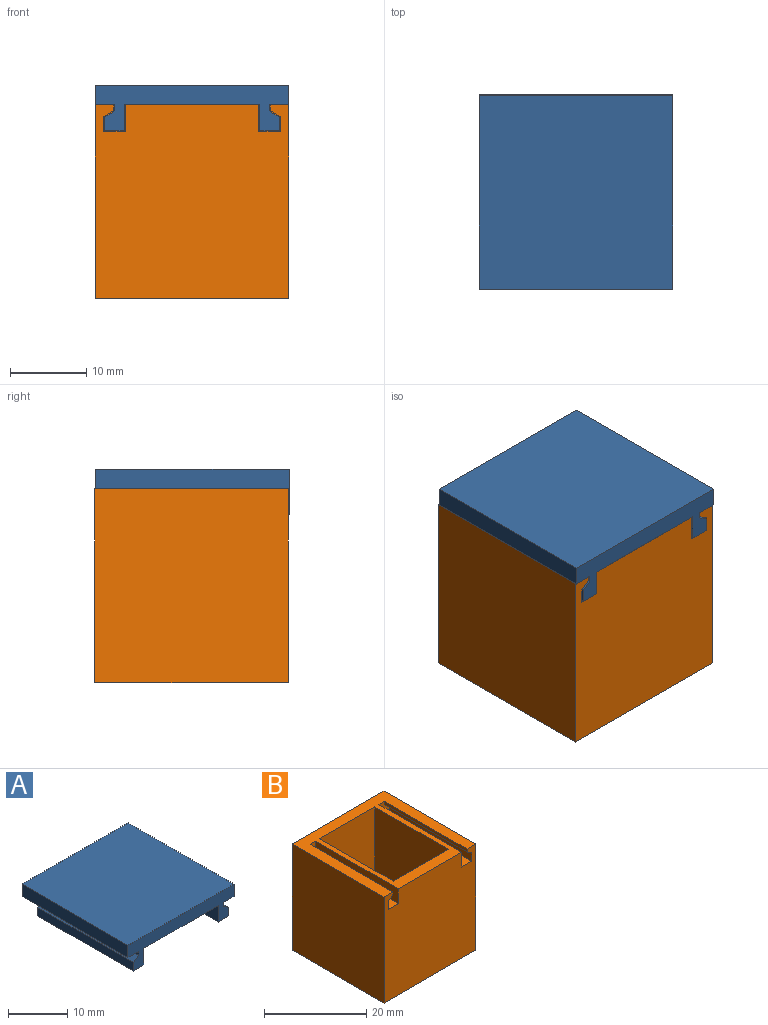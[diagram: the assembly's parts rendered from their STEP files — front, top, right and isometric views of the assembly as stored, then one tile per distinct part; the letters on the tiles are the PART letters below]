
ASSEMBLY  parts=2 mates=1
PART A: 18 faces, bbox 25.4x25.4x6 mm
  f0: plane 25.4x2.54mm, normal (0,1,0), area 64.5mm2, adj f1,f2,f4,f5
  f1: plane 25.4x2.54mm, normal (1,0,0), area 64.5mm2, adj f0,f3,f4,f5
  f2: plane 25.4x2.54mm, normal (-1,0,0), area 64.5mm2, adj f0,f3,f4,f5
  f3: plane 25.4x5.97mm, normal (0,-1,0), area 78.8mm2, adj f1,f2,f4,f5,f6,f7,f8,f9
  f4: plane 25.4x25.4mm, normal (0,0,-1), area 587.1mm2, adj f0,f1,f2,f3,f8,f9,f14,f15
  f5: plane 25.4x25.4mm, normal (0,0,1), area 645.2mm2, adj f0,f1,f2,f3
  f6: plane 22.86x1.78mm, normal (-1,0,0), area 40.6mm2, adj f3,f7,f10,f17
  f7: plane 22.86x2.54mm, normal (0,0,-1), area 58.1mm2, adj f3,f6,f8,f17
  f8: plane 22.86x3.43mm, normal (1,0,0), area 78.4mm2, adj f3,f4,f7,f17
  f9: plane 22.86x0.81mm, normal (-1,0,0), area 18.6mm2, adj f3,f4,f10,f17
  f10: plane 22.86x1.27mm, normal (-0.55,0,0.83), area 34.8mm2, adj f3,f6,f9,f17
  f11: plane 22.86x2.54mm, normal (0,0,-1), area 58.1mm2, adj f3,f12,f15,f16
  f12: plane 22.86x1.78mm, normal (1,0,0), area 40.6mm2, adj f3,f11,f13,f16
  f13: plane 22.86x1.27mm, normal (0.55,0,0.83), area 34.8mm2, adj f3,f12,f14,f16
  f14: plane 22.86x0.81mm, normal (1,0,0), area 18.6mm2, adj f3,f4,f13,f16
  f15: plane 22.86x3.43mm, normal (-1,0,0), area 78.4mm2, adj f3,f4,f11,f16
  f16: plane 3.43x2.54mm, normal (0,1,0), area 7.1mm2, adj f4,f11,f12,f13,f14,f15
  f17: plane 3.43x2.54mm, normal (0,1,0), area 7.1mm2, adj f4,f6,f7,f8,f9,f10
PART B: 23 faces, bbox 25.4x25.4x25.4 mm
  f0: plane 25.4x25.4mm, normal (0,1,0), area 645.2mm2, adj f2,f3,f4,f5
  f1: plane 25.4x25.4mm, normal (0,-1,0), area 628.3mm2, adj f2,f3,f4,f5,f11,f12,f13,f14
  f2: plane 25.4x25.4mm, normal (1,0,0), area 645.2mm2, adj f0,f1,f4,f5
  f3: plane 25.4x25.4mm, normal (-1,0,0), area 645.2mm2, adj f0,f1,f4,f5
  f4: plane 25.4x25.4mm, normal (0,0,-1), area 645.2mm2, adj f0,f1,f2,f3
  f5: plane 25.4x25.4mm, normal (0,0,1), area 266.4mm2, adj f0,f1,f2,f3,f6,f7,f8,f9
  f6: plane 22.86x20.29mm, normal (1,0,0), area 463.9mm2, adj f5,f7,f9,f10
  f7: plane 22.86x15.24mm, normal (0,1,0), area 348.4mm2, adj f5,f6,f8,f10
  f8: plane 22.86x20.29mm, normal (-1,0,0), area 463.9mm2, adj f5,f7,f9,f10
  f9: plane 22.86x15.24mm, normal (0,-1,0), area 348.4mm2, adj f5,f6,f8,f10
  f10: plane 20.29x15.24mm, normal (0,0,1), area 309.3mm2, adj f6,f7,f8,f9
  f11: plane 22.86x3.55mm, normal (1,0,0), area 81.1mm2, adj f1,f5,f12,f22
  f12: plane 22.86x2.79mm, normal (0,0,1), area 63.9mm2, adj f1,f11,f13,f22
  f13: plane 22.86x1.97mm, normal (-1,0,0), area 45.1mm2, adj f1,f12,f14,f22
  f14: plane 22.86x1.27mm, normal (-0.55,0,-0.84), area 34.8mm2, adj f1,f13,f15,f22
  f15: plane 22.86x0.74mm, normal (-1,0,0), area 16.9mm2, adj f1,f5,f14,f22
  f16: plane 22.86x1.97mm, normal (1,0,0), area 45.1mm2, adj f1,f17,f20,f21
  f17: plane 22.86x2.79mm, normal (0,0,1), area 63.9mm2, adj f1,f16,f18,f21
  f18: plane 22.86x3.55mm, normal (-1,0,0), area 81.1mm2, adj f1,f5,f17,f21
  f19: plane 22.86x0.74mm, normal (1,0,0), area 16.9mm2, adj f1,f5,f20,f21
  f20: plane 22.86x1.27mm, normal (0.55,0,-0.84), area 34.8mm2, adj f1,f16,f19,f21
  f21: plane 3.55x2.79mm, normal (0,-1,0), area 8.4mm2, adj f5,f16,f17,f18,f19,f20
  f22: plane 3.55x2.79mm, normal (0,-1,0), area 8.4mm2, adj f5,f11,f12,f13,f14,f15
PLACE A t=(-4.79,-8.06,7.46)mm
PLACE B t=(-4.79,-7.95,4.92)mm fixed
MATE slider A.f3 <-> B.f1  axis (0,-1,0) through (-17.49,-20.76,4.92)mm
